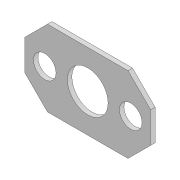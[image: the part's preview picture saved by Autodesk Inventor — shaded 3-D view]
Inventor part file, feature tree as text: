
AUTODESK INVENTOR PART (.ipt)
format: ipt  version: 2020 (Build 240168000, 168)  size: 108,544 bytes
history: native  units: mm
features: extrude x1, sketch x1
ambient origin geometry x8: Origin, YZ Plane, XZ Plane, XY Plane, X Axis, Y Axis, Z Axis, Center Point
bodies: Body1 (feature_tree)
feature tree (2):
  extrude  "Extrusion2"  Depth=168.0mm
  sketch  "Sketch1"  dims[d0=278.0mm d1=168.0mm d8=50.0mm d9=190.0mm d10=95.0mm d11=90.0mm d12=50.0mm d13=50.0mm d14=50.0mm d15=50.0mm d16=50.0mm d17=50.0mm d18=50.0mm d19=50.0mm d20=10.0mm d21=0.0mm]
